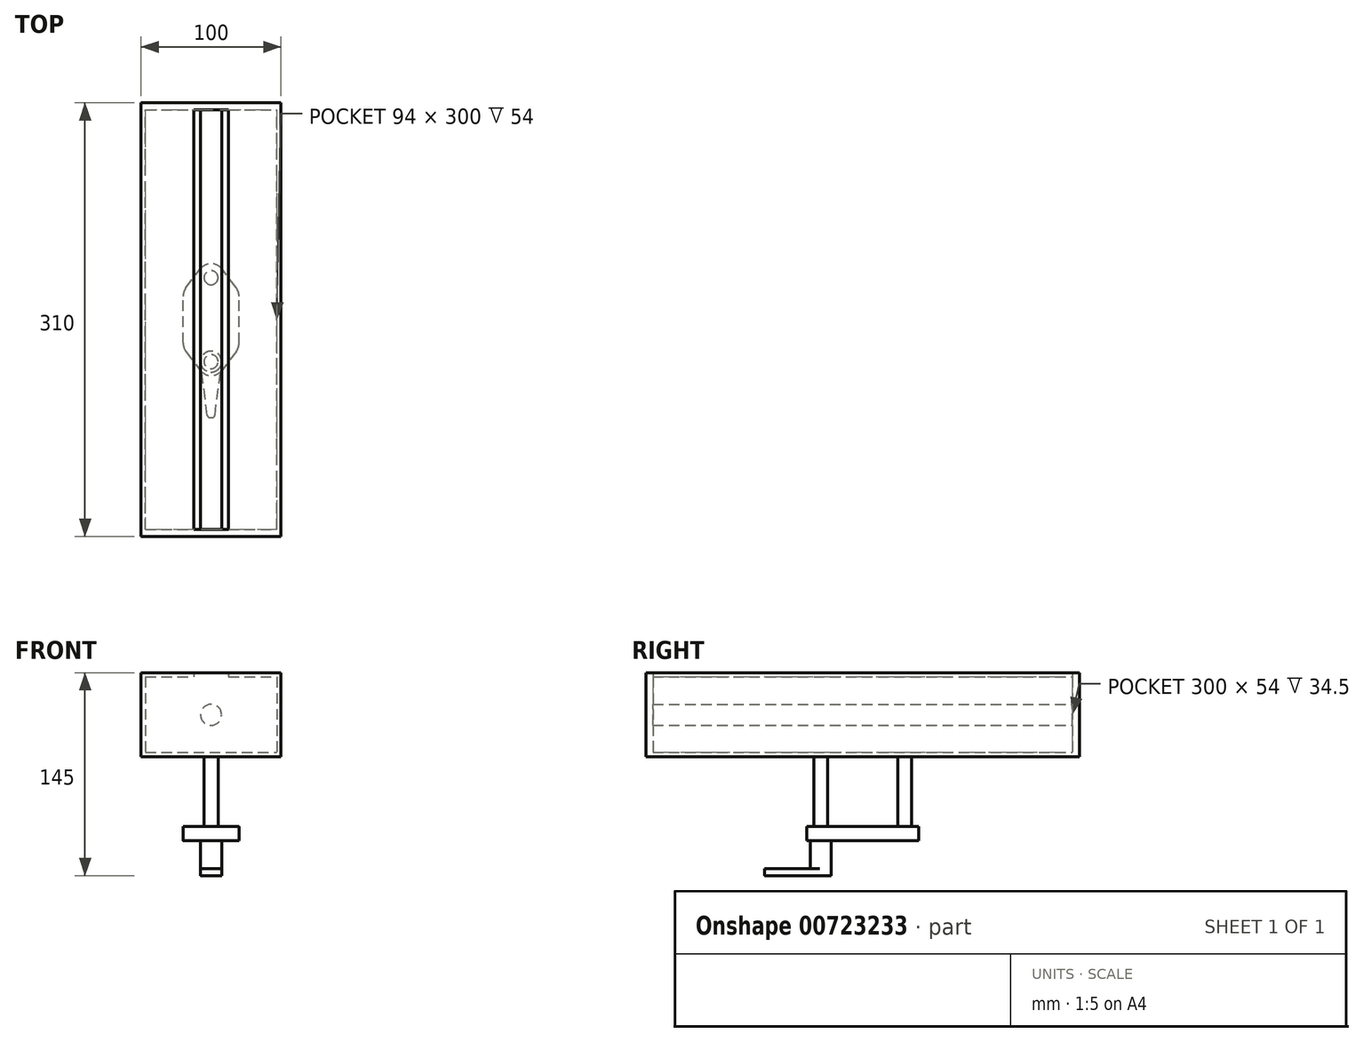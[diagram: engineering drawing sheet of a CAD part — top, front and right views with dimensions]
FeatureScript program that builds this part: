
annotation { "Feature Type Name" : "Feature", "Feature Type Description" : "" }
export const myFeature = defineFeature(function(context is Context, id is Id, definition is map)
    precondition{}
    {
        {
            var Q0;
            Q0=qCreatedBy(makeId("Front.planeOp"),FACE);
            var sketch = newSketch(context, id + "F0", { "sketchPlane" : qUnion([Q0])});
            skLineSegment(sketch, "E0.bottom", {"start": v(-50, 30) * mm, "end": v(-12.5, 30) * mm});
            skLineSegment(sketch, "E0.top", {"start": v(-50, -30) * mm, "end": v(50, -30) * mm});
            skLineSegment(sketch, "E0.left", {"start": v(-50, 30) * mm, "end": v(-50, -30) * mm});
            skLineSegment(sketch, "E0.right", {"start": v(50, 30) * mm, "end": v(50, -30) * mm});
            skCircle(sketch, "E1", {"center": v(0, 0) * mm, "radius": 7.5 * mm});
            skLineSegment(sketch, "E2.bottom", {"start": v(-47, 27) * mm, "end": v(-12.5, 27) * mm});
            skLineSegment(sketch, "E2.top", {"start": v(-47, -27) * mm, "end": v(47, -27) * mm});
            skLineSegment(sketch, "E2.left", {"start": v(-47, 27) * mm, "end": v(-47, -27) * mm});
            skLineSegment(sketch, "E2.right", {"start": v(47, 27) * mm, "end": v(47, -27) * mm});
            skLineSegment(sketch, "E3", {"start": v(-12.5, 30) * mm, "end": v(-12.5, 27) * mm});
            skLineSegment(sketch, "E4", {"start": v(12.5, 30) * mm, "end": v(12.5, 27) * mm});
            skLineSegment(sketch, "E5.trimOffspring", {"start": v(12.5, 27) * mm, "end": v(47, 27) * mm});
            skLineSegment(sketch, "E6.trimOffspring", {"start": v(12.5, 30) * mm, "end": v(50, 30) * mm});
            skSolve(sketch);
        }
        {
            var Q0;
            Q0 = qSketchRegion(id + "F0", true);
            extrude(context, id + "F1", {"entities" : qUnion([Q0]), "endBound" : BoundingType.SYMMETRIC, "depth" : 300 * mm, "offsetDistance" : 25 * mm});
        }
        {
            var Q0;
            Q0=makeQuery(id+"F1.opExtrude","CAP_FACE",FACE,{"disambiguationData":[OSD([sQuery(id+"F0.wireOp",EDGE,"E0.bottom"),sQuery(id+"F0.wireOp",EDGE,"E0.top"),sQuery(id+"F0.wireOp",EDGE,"E0.left"),sQuery(id+"F0.wireOp",EDGE,"E0.right"),sQuery(id+"F0.wireOp",EDGE,"E2.bottom"),sQuery(id+"F0.wireOp",EDGE,"E2.top"),sQuery(id+"F0.wireOp",EDGE,"E2.left"),sQuery(id+"F0.wireOp",EDGE,"E2.right"),sQuery(id+"F0.wireOp",EDGE,"E3"),sQuery(id+"F0.wireOp",EDGE,"E4"),sQuery(id+"F0.wireOp",EDGE,"E5.trimOffspring"),sQuery(id+"F0.wireOp",EDGE,"E6.trimOffspring")])],"isStart":false});
            var sketch = newSketch(context, id + "F2", { "sketchPlane" : qUnion([Q0])});
            skLineSegment(sketch, "E7.bottom", {"start": v(-50, 30) * mm, "end": v(50, 30) * mm});
            skLineSegment(sketch, "E7.top", {"start": v(-50, -30) * mm, "end": v(50, -30) * mm});
            skLineSegment(sketch, "E7.left", {"start": v(-50, 30) * mm, "end": v(-50, -30) * mm});
            skLineSegment(sketch, "E7.right", {"start": v(50, 30) * mm, "end": v(50, -30) * mm});
            skSolve(sketch);
        }
        {
            var Q0;
            Q0 = qSketchRegion(id + "F2", true);
            extrude(context, id + "F3", {"entities" : qUnion([Q0]), "operationType" : NewBodyOperationType.ADD, "depth" : 5 * mm, "offsetDistance" : 25 * mm});
        }
        {
            var Q0;
            Q0 = qSketchRegion(id + "F2", true);
            extrude(context, id + "F4", {"entities" : qUnion([Q0]), "operationType" : NewBodyOperationType.ADD, "depth" : 5 * mm, "offsetDistance" : 25 * mm});
        }
        {
            var Q0;
            Q0=makeQuery(id+"F1.opExtrude","CAP_FACE",FACE,{"disambiguationData":[OSD([sQuery(id+"F0.wireOp",EDGE,"E0.bottom"),sQuery(id+"F0.wireOp",EDGE,"E0.top"),sQuery(id+"F0.wireOp",EDGE,"E0.left"),sQuery(id+"F0.wireOp",EDGE,"E0.right"),sQuery(id+"F0.wireOp",EDGE,"E2.bottom"),sQuery(id+"F0.wireOp",EDGE,"E2.top"),sQuery(id+"F0.wireOp",EDGE,"E2.left"),sQuery(id+"F0.wireOp",EDGE,"E2.right"),sQuery(id+"F0.wireOp",EDGE,"E3"),sQuery(id+"F0.wireOp",EDGE,"E4"),sQuery(id+"F0.wireOp",EDGE,"E5.trimOffspring"),sQuery(id+"F0.wireOp",EDGE,"E6.trimOffspring")])],"isStart":true});
            var sketch = newSketch(context, id + "F5", { "sketchPlane" : qUnion([Q0])});
            skLineSegment(sketch, "E8.bottom", {"start": v(-50, 30) * mm, "end": v(50, 30) * mm});
            skLineSegment(sketch, "E8.top", {"start": v(-50, -30) * mm, "end": v(50, -30) * mm});
            skLineSegment(sketch, "E8.left", {"start": v(-50, 30) * mm, "end": v(-50, -30) * mm});
            skLineSegment(sketch, "E8.right", {"start": v(50, 30) * mm, "end": v(50, -30) * mm});
            skSolve(sketch);
        }
        {
            var Q0;
            Q0 = qSketchRegion(id + "F5", true);
            extrude(context, id + "F6", {"entities" : qUnion([Q0]), "operationType" : NewBodyOperationType.ADD, "depth" : 5 * mm, "offsetDistance" : 25 * mm});
        }
        {
            var Q0;
            Q0=makeQuery(id+"F6.boolean.opBoolean","MERGE",FACE,{"derivedFrom":[makeQuery(id+"F3.boolean.opBoolean","MERGE",FACE,{"derivedFrom":[makeQuery(id+"F1.opExtrude","SWEPT_FACE",FACE,{"disambiguationData":[OSD([sQuery(id+"F0.wireOp",EDGE,"E0.top")])]}),makeQuery(id+"F3.opExtrude","SWEPT_FACE",FACE,{"disambiguationData":[OSD([sQuery(id+"F2.wireOp",EDGE,"E7.top")])]})]}),makeQuery(id+"F6.opExtrude","SWEPT_FACE",FACE,{"disambiguationData":[OSD([sQuery(id+"F5.wireOp",EDGE,"E8.top")])]})]});
            var sketch = newSketch(context, id + "F7", { "sketchPlane" : qUnion([Q0])});
            skCircle(sketch, "E9", {"center": v(0, 30) * mm, "radius": 5 * mm});
            skCircle(sketch, "E10", {"center": v(0, -30) * mm, "radius": 5 * mm});
            skSolve(sketch);
        }
        {
            var Q0;
            Q0 = qSketchRegion(id + "F7", true);
            extrude(context, id + "F8", {"entities" : qUnion([Q0]), "operationType" : NewBodyOperationType.ADD, "depth" : 50 * mm, "offsetDistance" : 25 * mm});
        }
        {
            var Q0;
            Q0=makeQuery(id+"F8.opExtrude","CAP_FACE",FACE,{"disambiguationData":[OSD([sQuery(id+"F7.wireOp",EDGE,"E9")])],"isStart":false});
            var sketch = newSketch(context, id + "F9", { "sketchPlane" : qUnion([Q0])});
            skArc(sketch, "E11", {"start": v(8, 36) * mm, "mid": v(0, 40) * mm, "end": v(-8, 36) * mm});
            skArc(sketch, "E12", {"start": v(-8, -36) * mm, "mid": v(0, -40) * mm, "end": v(8, -36) * mm});
            skLineSegment(sketch, "E13.left", {"start": v(-20, 16.67) * mm, "end": v(-20, -16.67) * mm});
            skLineSegment(sketch, "E13.right", {"start": v(20, 16.67) * mm, "end": v(20, -16.67) * mm});
            skLineSegment(sketch, "E14", {"start": v(-18, 22.67) * mm, "end": v(-8, 36) * mm});
            skLineSegment(sketch, "E15", {"start": v(18, 22.67) * mm, "end": v(8, 36) * mm});
            skLineSegment(sketch, "E16", {"start": v(-18, -22.67) * mm, "end": v(-8, -36) * mm});
            skLineSegment(sketch, "E17", {"start": v(18, -22.67) * mm, "end": v(8, -36) * mm});
            skPoint(sketch, "E18.visualSharp", {"position": v(-20, 20) * mm});
            skArc(sketch, "E18.filletArc", {"start": v(-18, 22.67) * mm, "mid": v(-19.49, 19.83) * mm, "end": v(-20, 16.67) * mm});
            skPoint(sketch, "E19.visualSharp", {"position": v(-20, -20) * mm});
            skArc(sketch, "E19.filletArc", {"start": v(-20, -16.67) * mm, "mid": v(-19.49, -19.83) * mm, "end": v(-18, -22.67) * mm});
            skPoint(sketch, "E20.visualSharp", {"position": v(20, -20) * mm});
            skArc(sketch, "E20.filletArc", {"start": v(18, -22.67) * mm, "mid": v(19.49, -19.83) * mm, "end": v(20, -16.67) * mm});
            skPoint(sketch, "E21.visualSharp", {"position": v(20, 20) * mm});
            skArc(sketch, "E21.filletArc", {"start": v(20, 16.67) * mm, "mid": v(19.49, 19.83) * mm, "end": v(18, 22.67) * mm});
            skSolve(sketch);
        }
        {
            var Q0;
            Q0=makeQuery(id+"F9.imprint","IMPRINT",FACE,{"disambiguationData":[TD([[makeQuery(id+"F9.imprint","IMPRINT",EDGE,{"derivedFrom":sQuery(id+"F9.wireOp",EDGE,"E11")}),1.0]])]});
            var Q1;
            Q1=makeQuery(id+"F9.imprint","IMPRINT",FACE,{"disambiguationData":[TD([[makeQuery(id+"F9.imprint","IMPRINT",EDGE,{"derivedFrom":makeQuery(id+"F8.opExtrude","CAP_EDGE",EDGE,{"disambiguationData":[OSD([sQuery(id+"F7.wireOp",EDGE,"E9")])],"isStart":false})}),1.0]])]});
            extrude(context, id + "F10", {"entities" : qUnion([Q0, Q1]), "operationType" : NewBodyOperationType.ADD, "depth" : 10 * mm, "offsetDistance" : 25 * mm});
        }
        {
            var Q0;
            Q0=makeQuery(id+"F10.opExtrude","CAP_FACE",FACE,{"disambiguationData":[OSD([sQuery(id+"F9.wireOp",EDGE,"E11"),sQuery(id+"F9.wireOp",EDGE,"E12"),sQuery(id+"F9.wireOp",EDGE,"E13.left"),sQuery(id+"F9.wireOp",EDGE,"E13.right"),sQuery(id+"F9.wireOp",EDGE,"E14"),sQuery(id+"F9.wireOp",EDGE,"E15"),sQuery(id+"F9.wireOp",EDGE,"E16"),sQuery(id+"F9.wireOp",EDGE,"E17"),sQuery(id+"F9.wireOp",EDGE,"E18.filletArc"),sQuery(id+"F9.wireOp",EDGE,"E19.filletArc"),sQuery(id+"F9.wireOp",EDGE,"E20.filletArc"),sQuery(id+"F9.wireOp",EDGE,"E21.filletArc")])],"isStart":false});
            var sketch = newSketch(context, id + "F11", { "sketchPlane" : qUnion([Q0])});
            skCircle(sketch, "E22", {"center": v(0, 30) * mm, "radius": 7.5 * mm});
            skSolve(sketch);
        }
        {
            var Q0;
            Q0 = qSketchRegion(id + "F11", true);
            extrude(context, id + "F12", {"entities" : qUnion([Q0]), "operationType" : NewBodyOperationType.ADD, "depth" : 25 * mm, "offsetDistance" : 25 * mm});
        }
        {
            var Q0;
            Q0=makeQuery(id+"F12.opExtrude","CAP_FACE",FACE,{"disambiguationData":[OSD([sQuery(id+"F11.wireOp",EDGE,"E22")])],"isStart":false});
            var sketch = newSketch(context, id + "F13", { "sketchPlane" : qUnion([Q0])});
            skArc(sketch, "E23", {"start": v(-7.44, 30.94) * mm, "mid": v(0, 22.5) * mm, "end": v(7.44, 30.94) * mm});
            skLineSegment(sketch, "E24.top", {"start": v(-0.74, 70.04) * mm, "end": v(0.74, 70.04) * mm});
            skLineSegment(sketch, "E25", {"start": v(-2.72, 68.3) * mm, "end": v(-7.44, 30.94) * mm});
            skLineSegment(sketch, "E26", {"start": v(2.72, 68.3) * mm, "end": v(7.44, 30.94) * mm});
            skPoint(sketch, "E27.visualSharp", {"position": v(-2.5, 70.04) * mm});
            skArc(sketch, "E27.filletArc", {"start": v(-0.74, 70.04) * mm, "mid": v(-2.06, 69.54) * mm, "end": v(-2.72, 68.3) * mm});
            skPoint(sketch, "E28.visualSharp", {"position": v(2.5, 70.04) * mm});
            skArc(sketch, "E28.filletArc", {"start": v(2.72, 68.3) * mm, "mid": v(2.06, 69.54) * mm, "end": v(0.74, 70.04) * mm});
            skSolve(sketch);
        }
        {
            var Q0;
            Q0 = qSketchRegion(id + "F13", true);
            extrude(context, id + "F14", {"entities" : qUnion([Q0]), "operationType" : NewBodyOperationType.ADD, "oppositeDirection" : true, "depth" : 5 * mm, "offsetDistance" : 25 * mm});
        }
    });
